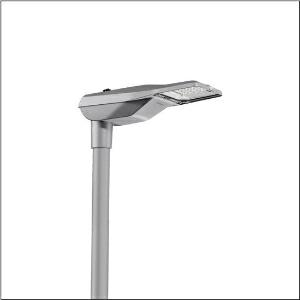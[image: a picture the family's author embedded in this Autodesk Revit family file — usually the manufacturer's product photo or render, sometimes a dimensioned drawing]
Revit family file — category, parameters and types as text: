
# Revit family: streetlight_sl_21_micro___st1_0a_5xe1d33s08db_38a0
name_source: partatom
category: Lighting Fixtures
units: mm (PartAtom-declared; Revit-internal decimal feet)

## family parameters
Cut with Voids When Loaded = No
Host = Face
Light Source = No
Part Type = Normal
Room Calculation Point = No
Round Connector Dimension = Use Diameter
Shared = No

## types (1)
- --- (1 x LED, 5110 lm, 39.1 W, 3000K)
    Apparent Load = 39 VA
    CIE Flux Codes = 37 72 97 100 100
    Color Rendering = 70
    Color Temperature = 3000K
    Default Elevation = 1800 mm
    Description = Streetlight SL 21 micro, mast luminaire, primary light control with lens, of PMMA, primary optical cover: cover, of toughened safety glass, transparent, light distribution: ST1.0a, light emission: direct distribution, primary light characteristic: asymmetric, installation type: side-entry, post-top, LED, High Power LED, rated luminous flux: 5.110lm, luminous efficacy: 131lm/W, light colour: 730, colour temperature: 3000K, control: flexible luminous flux parameterisation, time-dependent luminous flux control, constant luminous flux control, overheat protection, presetting dimming logarithmic, mains connection: 220..240V, AC, 50/60Hz, start of lifetime: 39W, end of service life: 41W, reduction: 18W, luminaire housing, of diecast aluminium, powder-coated, Siteco® metallic grey (DB 702S), corrosivity category C5 mid according to DIN EN ISO 12944, please order mast flange separately, inclination adjustable: 0°, 5°, 10°, 15°, sealing non-destructively replaceable, multi-level sealing system, length: 528mm, width: 235mm, height: 110mm, mast flange for spigot size: 42mm (side-entry): 5XC10008XM4, 60/48mm (side-entry/post-top): 5XC10108XM2, 76/60mm (side-entry/post-top): 5XC10108XM1, Smart Interface above, protection rating (complete): IP66, insulation class (complete): insulation class II (safety insulation), certification: CE, ENEC, ENEC+, VDE, impact resistance: IK09, permissible operating ambient temperature for outdoor applications: -40..+50°C, standard-compliant lighting for roads and squares, packaging unit: 1 piece

Light Distribution: ST1.0a
    Height = 110 mm
    Lamp = 1 x LED
    Lamp Light Flux = 5110 lm
    Lamp Power = 39.1 W
    Lamp count = 1
    Length = 528 mm
    Luminous efficacy = 131 lm/W
    Manufacturer = Siteco
    ModVariant = No
    Model = 5XE1D33S08DB
    Number of Poles = 1
    OnlyDefault = Yes
    Power Factor = 1
    Product Name = Streetlight SL 21 micro | ST1.0a
    Product group = mast luminaire | pylon top
    ProductGroupID = 6100
    Protection Class = Protection class II
    Protection Degree = IP 66
    RLX_Detail_Level = 1
    RLX_Emergency_Light_Flux = 0 lm
    RLX_Emergency_Type = 0
    RLX_Emergency_Type_DB = No
    RlxData = <blob elided: 99261 chars, md5=36df09c9>
    Socket = socket
    Standby Power = 0 W
    System Light Flux = 5110 lm
    System Power = 39 W
    Type Comments = factory setting: luminous flux: 100 % | dim-lin: 254 | 765 mA
    Type Image = l_1277292.jpg
    URL = http://relux.com
    VarID = @adj_088139
    Voltage = 0 V
    Weight = 0.00 kg
    Width = 235 mm

## geometry (parser evidence)
native form markers: Blend x4, Sweep x9
no freeform markers — native parametric forms only
